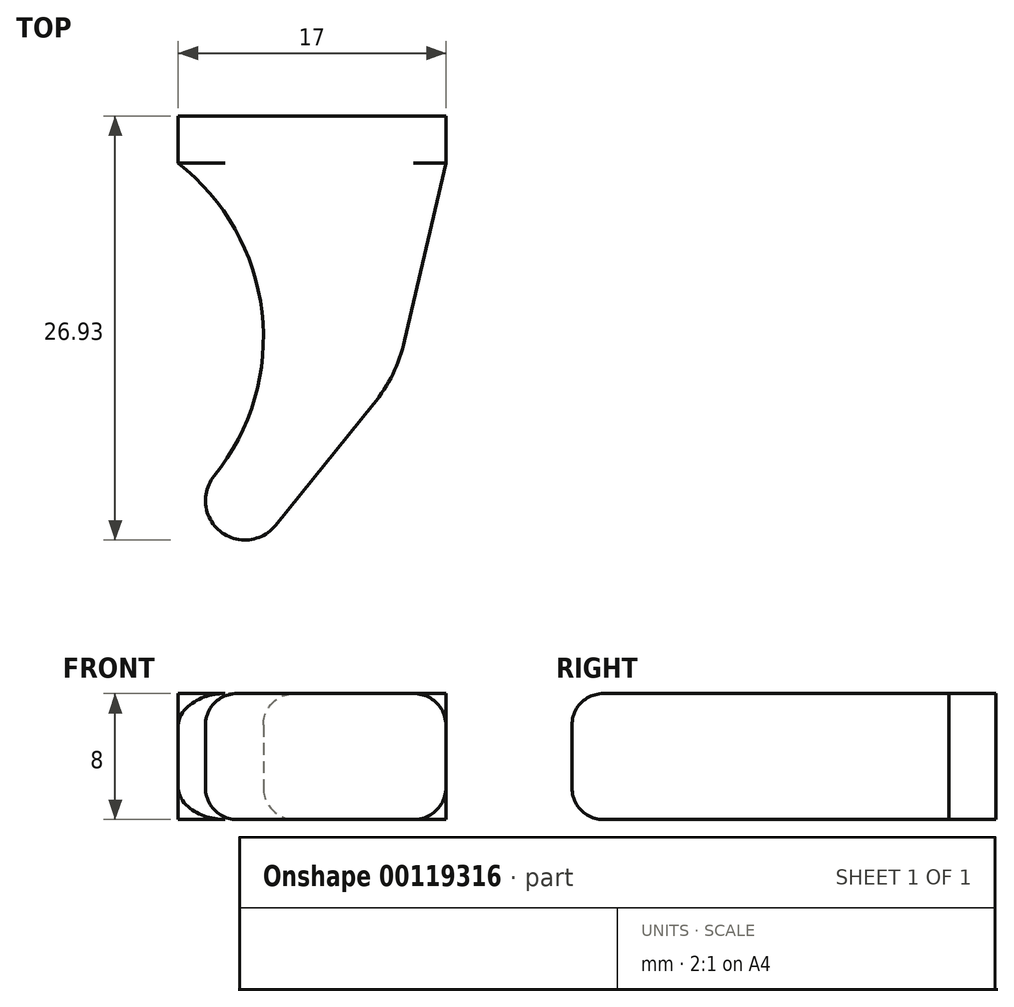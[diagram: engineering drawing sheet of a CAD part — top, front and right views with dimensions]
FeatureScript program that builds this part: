
annotation { "Feature Type Name" : "Feature", "Feature Type Description" : "" }
export const myFeature = defineFeature(function(context is Context, id is Id, definition is map)
    precondition{}
    {
        {
            var Q0;
            Q0=qCreatedBy(makeId("Top.planeOp"),FACE);
            var sketch = newSketch(context, id + "F0", { "sketchPlane" : qUnion([Q0])});
            skLineSegment(sketch, "E0", {"start": v(34.3, 0) * mm, "end": v(31.17, -13.5) * mm});
            skLineSegment(sketch, "E1", {"start": v(31.17, -13.5) * mm, "end": v(23.48, -23) * mm});
            skArc(sketch, "E2", {"start": v(19.6, -19.86) * mm, "mid": v(22.62, -9.45) * mm, "end": v(17.3, 0) * mm});
            skArc(sketch, "E3", {"start": v(19.6, -19.86) * mm, "mid": v(19.97, -23.37) * mm, "end": v(23.48, -23) * mm});
            skLineSegment(sketch, "E4", {"start": v(17.3, 0) * mm, "end": v(34.3, 0) * mm});
            skSolve(sketch);
        }
        {
            var Q0;
            Q0=qSketchRegion(id+"F0",true);
            extrude(context, id + "F1", {"entities" : qUnion([Q0]), "endBound" : BoundingType.SYMMETRIC, "depth" : 8 * mm});
        }
        {
            var Q0;
            Q0=makeQuery(id+"F1.opExtrude","SWEPT_EDGE",EDGE,{"disambiguationData":[OSD([sQuery(id+"F0.wireOp",EDGE,"E0"),sQuery(id+"F0.wireOp",EDGE,"E1")])]});
            fillet(context, id + "F2", {"entities" : qUnion([Q0]), "radius" : 10 * mm, "tangentPropagation" : true, "allowEdgeOverflow" : false});
        }
        {
            var Q0;
            Q0=makeQuery(id+"F1.opExtrude","CAP_EDGE",EDGE,{"disambiguationData":[OSD([sQuery(id+"F0.wireOp",EDGE,"E0")])],"isStart":false});
            var Q1;
            {var subQ0=sQuery(id+"F0.wireOp",EDGE,"E1");var subQ1=sQuery(id+"F0.wireOp",EDGE,"E0");Q1=makeQuery(id+"F2.opFillet","BLEND_EDGE",EDGE,{"blendedFrom":[makeQuery(id+"F1.opExtrude","SWEPT_EDGE",EDGE,{"disambiguationData":[OSD([subQ1,subQ0])]}),makeQuery(id+"F1.opExtrude","CAP_FACE",FACE,{"disambiguationData":[OSD([subQ1,subQ0,sQuery(id+"F0.wireOp",EDGE,"7X7qKE2I-nNr8-b8lX-uq4A-mIGdcvM5fNAC"),sQuery(id+"F0.wireOp",EDGE,"3254c177-f137-4f4f-9550-8d5c5fa8e2b2.0"),sQuery(id+"F0.wireOp",EDGE,"E2"),sQuery(id+"F0.wireOp",EDGE,"E3"),sQuery(id+"F0.wireOp",EDGE,"4dd9163c-d638-4e9a-84bb-52db589eff29.0")])],"isStart":false})],"blendedInto":[makeQuery(id+"F1.opExtrude","CAP_FACE",FACE,{"disambiguationData":[OSD([subQ1,subQ0,sQuery(id+"F0.wireOp",EDGE,"7X7qKE2I-nNr8-b8lX-uq4A-mIGdcvM5fNAC"),sQuery(id+"F0.wireOp",EDGE,"3254c177-f137-4f4f-9550-8d5c5fa8e2b2.0"),sQuery(id+"F0.wireOp",EDGE,"E2"),sQuery(id+"F0.wireOp",EDGE,"E3"),sQuery(id+"F0.wireOp",EDGE,"4dd9163c-d638-4e9a-84bb-52db589eff29.0")])],"isStart":false})]});}
            var Q2;
            Q2=makeQuery(id+"F1.opExtrude","CAP_EDGE",EDGE,{"disambiguationData":[OSD([sQuery(id+"F0.wireOp",EDGE,"E1")])],"isStart":false});
            var Q3;
            Q3=makeQuery(id+"F1.opExtrude","CAP_EDGE",EDGE,{"disambiguationData":[OSD([sQuery(id+"F0.wireOp",EDGE,"E3")])],"isStart":false});
            var Q4;
            Q4=makeQuery(id+"F1.opExtrude","CAP_EDGE",EDGE,{"disambiguationData":[OSD([sQuery(id+"F0.wireOp",EDGE,"E2")])],"isStart":false});
            var Q5;
            Q5=makeQuery(id+"F1.opExtrude","CAP_EDGE",EDGE,{"disambiguationData":[OSD([sQuery(id+"F0.wireOp",EDGE,"E2")])],"isStart":true});
            var Q6;
            Q6=makeQuery(id+"F1.opExtrude","CAP_EDGE",EDGE,{"disambiguationData":[OSD([sQuery(id+"F0.wireOp",EDGE,"E3")])],"isStart":true});
            var Q7;
            Q7=makeQuery(id+"F1.opExtrude","CAP_EDGE",EDGE,{"disambiguationData":[OSD([sQuery(id+"F0.wireOp",EDGE,"E1")])],"isStart":true});
            var Q8;
            {var subQ0=sQuery(id+"F0.wireOp",EDGE,"E1");var subQ1=sQuery(id+"F0.wireOp",EDGE,"E0");Q8=makeQuery(id+"F2.opFillet","BLEND_EDGE",EDGE,{"blendedFrom":[makeQuery(id+"F1.opExtrude","SWEPT_EDGE",EDGE,{"disambiguationData":[OSD([subQ1,subQ0])]}),makeQuery(id+"F1.opExtrude","CAP_FACE",FACE,{"disambiguationData":[OSD([subQ1,subQ0,sQuery(id+"F0.wireOp",EDGE,"7X7qKE2I-nNr8-b8lX-uq4A-mIGdcvM5fNAC"),sQuery(id+"F0.wireOp",EDGE,"3254c177-f137-4f4f-9550-8d5c5fa8e2b2.0"),sQuery(id+"F0.wireOp",EDGE,"E2"),sQuery(id+"F0.wireOp",EDGE,"E3"),sQuery(id+"F0.wireOp",EDGE,"4dd9163c-d638-4e9a-84bb-52db589eff29.0")])],"isStart":true})],"blendedInto":[makeQuery(id+"F1.opExtrude","CAP_FACE",FACE,{"disambiguationData":[OSD([subQ1,subQ0,sQuery(id+"F0.wireOp",EDGE,"7X7qKE2I-nNr8-b8lX-uq4A-mIGdcvM5fNAC"),sQuery(id+"F0.wireOp",EDGE,"3254c177-f137-4f4f-9550-8d5c5fa8e2b2.0"),sQuery(id+"F0.wireOp",EDGE,"E2"),sQuery(id+"F0.wireOp",EDGE,"E3"),sQuery(id+"F0.wireOp",EDGE,"4dd9163c-d638-4e9a-84bb-52db589eff29.0")])],"isStart":true})]});}
            var Q9;
            Q9=makeQuery(id+"F1.opExtrude","CAP_EDGE",EDGE,{"disambiguationData":[OSD([sQuery(id+"F0.wireOp",EDGE,"E0")])],"isStart":true});
            fillet(context, id + "F3", {"entities" : qUnion([Q0, Q1, Q2, Q3, Q4, Q5, Q6, Q7, Q8, Q9]), "radius" : 2 * mm, "tangentPropagation" : true, "allowEdgeOverflow" : false});
        }
        {
            var Q0;
            Q0=makeQuery(id+"F1.opExtrude","SWEPT_FACE",FACE,{"disambiguationData":[OSD([sQuery(id+"F0.wireOp",EDGE,"E4")])]});
            var sketch = newSketch(context, id + "F4", { "sketchPlane" : qUnion([Q0])});
            skLineSegment(sketch, "E5", {"start": v(-34.3, -4) * mm, "end": v(-34.3, 4) * mm});
            skLineSegment(sketch, "E6", {"start": v(-34.3, 4) * mm, "end": v(-17.3, 4) * mm});
            skLineSegment(sketch, "E7.MirrorCS", {"start": v(-34.3, -4) * mm, "end": v(-17.3, -4) * mm});
            skLineSegment(sketch, "E8", {"start": v(-17.3, -4) * mm, "end": v(-17.3, 4) * mm});
            skPoint(sketch, "E9.orphan", {"position": v(-20.28, -4) * mm});
            skSolve(sketch);
        }
        {
            var Q0;
            Q0 = qSketchRegion(id + "F4", true);
            extrude(context, id + "F5", {"entities" : qUnion([Q0]), "operationType" : NewBodyOperationType.ADD, "depth" : 3 * mm});
        }
    });
